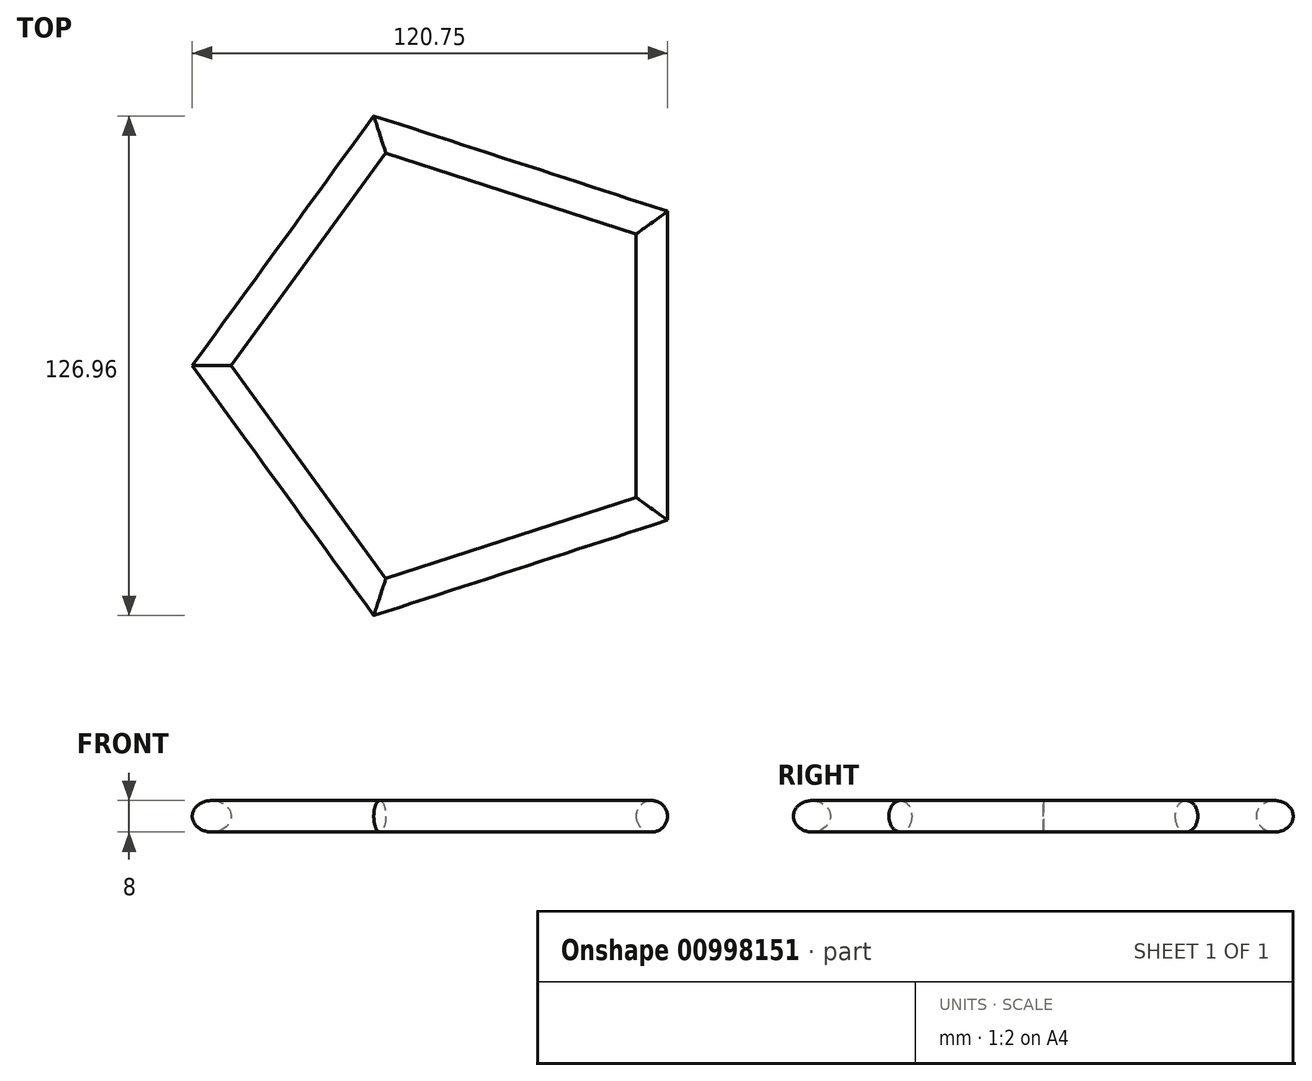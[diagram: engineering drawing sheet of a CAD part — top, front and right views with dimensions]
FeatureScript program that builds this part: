
annotation { "Feature Type Name" : "Feature", "Feature Type Description" : "" }
export const myFeature = defineFeature(function(context is Context, id is Id, definition is map)
    precondition{}
    {
        {
            var Q0;
            Q0=qCreatedBy(makeId("Top.planeOp"),FACE);
            var sketch = newSketch(context, id + "F0", { "sketchPlane" : qUnion([Q0])});
            skCircle(sketch, "E0.cCircle", {"center": v(0, 0) * mm, "radius": 50 * mm, "construction": true});
            skLineSegment(sketch, "E0.0", {"start": v(50, 36.33) * mm, "end": v(50, -36.33) * mm});
            skLineSegment(sketch, "E0.1", {"start": v(50, -36.33) * mm, "end": v(-19.1, -58.78) * mm});
            skLineSegment(sketch, "E0.2", {"start": v(-19.1, -58.78) * mm, "end": v(-61.8, 0) * mm});
            skLineSegment(sketch, "E0.3", {"start": v(-61.8, 0) * mm, "end": v(-19.1, 58.78) * mm});
            skLineSegment(sketch, "E0.4", {"start": v(-19.1, 58.78) * mm, "end": v(50, 36.33) * mm});
            skPoint(sketch, "E0.0.midPoint", {"position": v(50, 0) * mm});
            skSolve(sketch);
        }
        {
            var Q0;
            Q0=qCreatedBy(makeId("Front.planeOp"),FACE);
            var sketch = newSketch(context, id + "F1", { "sketchPlane" : qUnion([Q0])});
            skCircle(sketch, "E1", {"center": v(50, 0) * mm, "radius": 4 * mm});
            skSolve(sketch);
        }
        {
            var Q0;
            Q0=makeQuery(id+"F1.imprint","IMPRINT",FACE,{"disambiguationData":[TD([[makeQuery(id+"F1.imprint","IMPRINT",EDGE,{"derivedFrom":sQuery(id+"F1.wireOp",EDGE,"E1")}),1.0]])]});
            var Q1;
            Q1=sQuery(id+"F0.wireOp",EDGE,"E0.1");
            var Q2;
            Q2=sQuery(id+"F0.wireOp",EDGE,"E0.0");
            var Q3;
            Q3=sQuery(id+"F0.wireOp",EDGE,"E0.4");
            var Q4;
            Q4=sQuery(id+"F0.wireOp",EDGE,"E0.3");
            var Q5;
            Q5=sQuery(id+"F0.wireOp",EDGE,"E0.2");
            sweep(context, id + "F2", {"profiles" : qUnion([Q0]), "path" : qUnion([Q1, Q2, Q3, Q4, Q5])});
        }
    });
